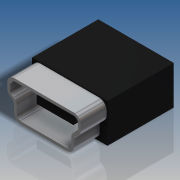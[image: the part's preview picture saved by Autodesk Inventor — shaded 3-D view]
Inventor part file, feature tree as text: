
AUTODESK INVENTOR PART (.ipt)
format: ipt  version: 2016 SP2 (Build 200236200, 236)  size: 282,624 bytes
history: native  units: in
note: dims shown in document units (in); Inventor stores cm internally (conversion verified against a paired STEP export)
features: extrude x6, sketch x4, projected_geometry x3, other x1
ambient origin geometry x8: Origin, YZ Plane, XZ Plane, XY Plane, X Axis, Y Axis, Z Axis, Center Point
bodies: Solid1 (feature_tree)
feature tree (14):
  extrude  "Extrusion1"  Depth=0.315in
  sketch  "Sketch3"  dims[d2=0.2835in d3=0.0in d4=0.2566in]
  extrude  "Extrusion2"  Depth=0.2566in
  extrude  "Extrusion3"  Depth=0.0118in
  extrude  "Extrusion4"  Depth=0.1417in TaperAngle=0.0deg
  extrude  "Extrusion5"  Depth=0.1417in
  extrude  "Extrusion6"  Depth=0.1417in
  sketch  "Sketch2"  dims[d0=0.1575in d1=0.315in]
  sketch  "Sketch4"  dims[d5=0.0315in d8=0.0118in]
  sketch  "Sketch5"  dims[d9=60.0deg d10=0.1102in d11=0.0in d12=0.1575in d13=0.0315in d14=0.063in d15=0.0in d16=0.1417in d17=0.0in d18=0.0197in d19=0.0079in d20=0.0004in d21=0.0in d22=0.0039in d24=0.0039in d25=0.0004in d26=0.0in]
  projected_geometry  "Projected Loop1"
  projected_geometry  "Projected Loop2"
  projected_geometry  "Projected Loop3"
  other  "Srf1"
